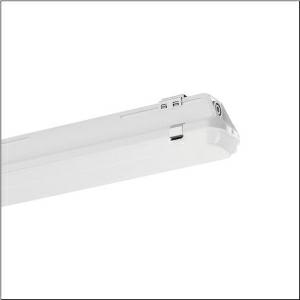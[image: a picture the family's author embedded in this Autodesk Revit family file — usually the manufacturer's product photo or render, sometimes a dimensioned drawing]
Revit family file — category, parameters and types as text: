
# Revit family: monsun_21_51fb20ml460k
name_source: partatom
category: Lighting Fixtures
units: mm (PartAtom-declared; Revit-internal decimal feet)

## family parameters
Cut with Voids When Loaded = No
Host = Face
Light Source = No
Part Type = Normal
Room Calculation Point = No
Round Connector Dimension = Use Diameter
Shared = No

## types (1)
- --- (1 x LED, 6030 lm, 37 W, 4000K)
    Apparent Load = 37 VA
    CIE Flux Codes = 45 75 93 94 100
    Color Rendering = 80
    Color Temperature = 4000K
    Default Elevation = 1800 mm
    Description = Monsun 21, damp-proof luminaire, chain hanger, primary optical cover: enclosure, of PC, light emission: direct distribution, primary light characteristic: symmetric, installation type: suspended mounting, surface-mounted, horizontal mounting, vertical mounting, LED, rated luminous flux: 6.030lm, luminous efficacy: 163lm/W, light colour: 840, colour temperature: 4000K, control gear: ON/OFF Multilumen, with terminal, 3-pole, max. 2.5mm², mains connection: 220..240V, AC, 50/60Hz, rated input power: 37W, housing, of glass-fibre reinforced plastic, uncoated, bright grey, incl. chain hanger, length: 1.299mm, width: 90mm, height: 88mm, clip for enclosure, of stainless steel (V2A), ceiling mounting element, of stainless steel (V2A), chain hanger, of stainless steel (V2A), protection rating (complete): IP66, insulation class (complete): insulation class I (protective earthing), certification: CE, ENEC, VDE, UKCA, protection symbol: D, impact resistance: IK04, permissible operating ambient temperature: -25..+35°C, standard: EN 50419, EN 60598-2-1, corresponds to IFS (International Featured Standards) requirements for safety and quality in the food industry, for indoor or canopied outdoor use, no direct snow, no direct sun, no direct rain, LABS conformity tested according to VDMA 24364:2018-05, contact your sales advisor before using the luminaires in applications with unclear chemical exposure, large temperature fluctuations or condensation-forming humidity, packaging unit: 1 piece
    Height = 88 mm
    Lamp = 1 x LED
    Lamp Light Flux = 6030 lm
    Lamp Power = 37 W
    Lamp count = 1
    Length = 1299 mm
    Luminous efficacy = 163 lm/W
    Manufacturer = Siteco
    ModVariant = No
    Model = 51FB20ML460K
    Mounting Place = Ceiling
    Mounting Type = Surface mounted
    Number of Poles = 1
    OnlyDefault = Yes
    Power Factor = 1
    Product Name = Monsun 21
    Product group = damp-proof luminaire
    ProductGroupID = 300
    Protection Class = Protection class I
    Protection Degree = IP 66
    RLX_Detail_Level = 1
    RLX_Emergency_Light_Flux = 0 lm
    RLX_Emergency_Type = 0
    RLX_Emergency_Type_DB = No
    RlxData = <blob elided: 91149 chars, md5=7e24f995>
    Socket = socket
    Standby Power = 0 W
    System Light Flux = 6030 lm
    System Power = 37 W
    Type Comments = factory setting: luminous flux: 100 % | (A | C | E) | 86 mA
    Type Image = l_1319656.jpg
    URL = http://relux.com
    VarID = @adj_049533
    Voltage = 0 V
    Weight = 0.00 kg
    Width = 90 mm

## geometry (parser evidence)
native form markers: Blend x4, Sweep x12
no freeform markers — native parametric forms only
